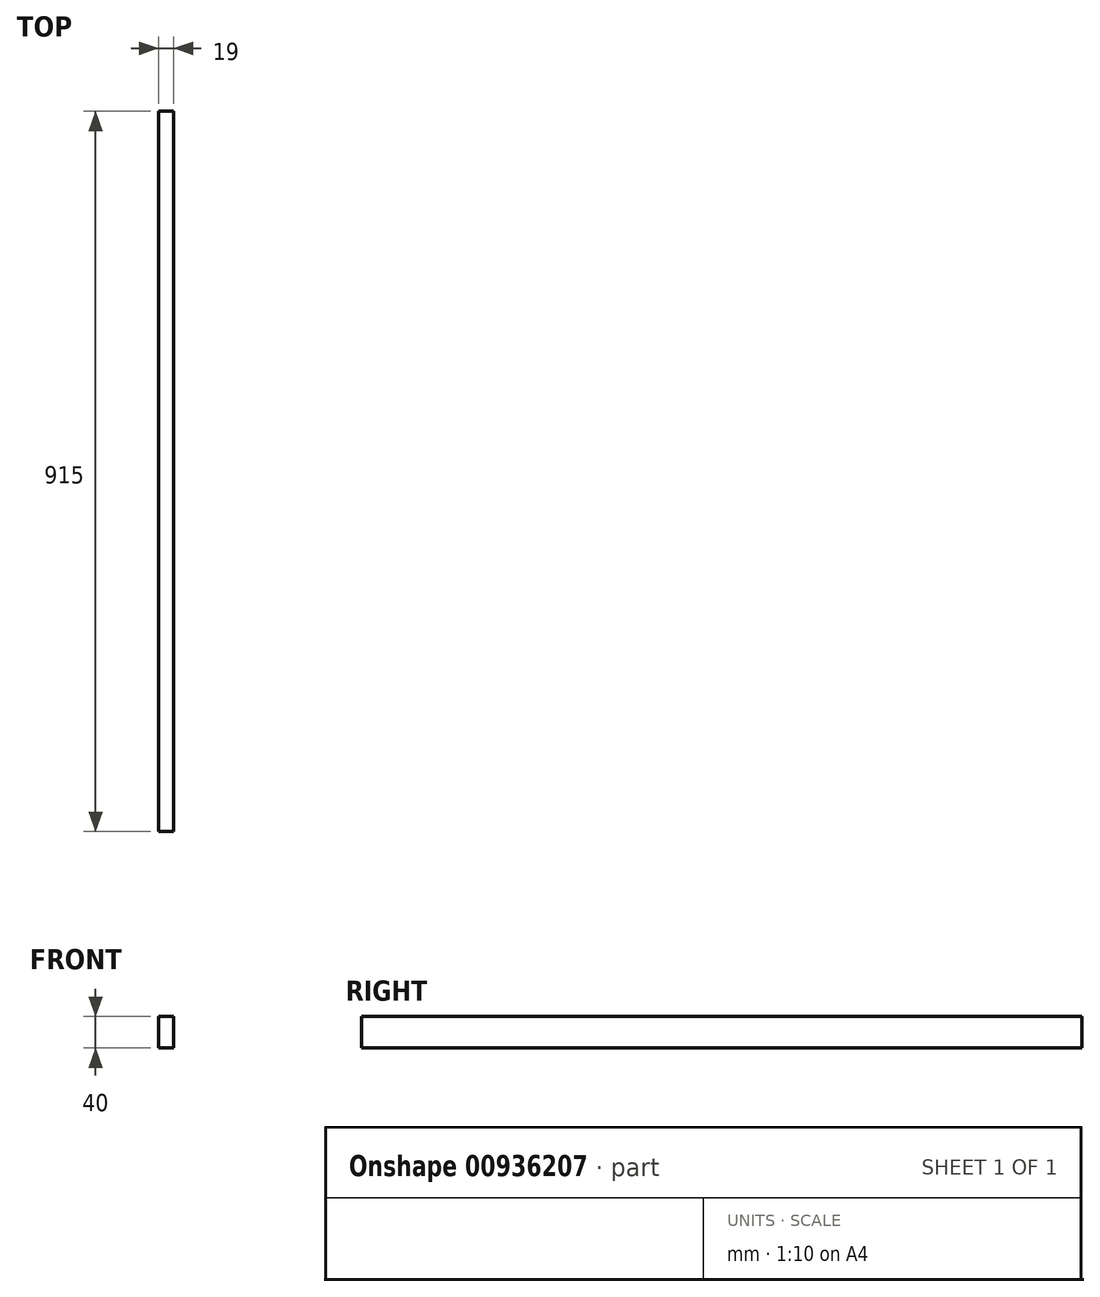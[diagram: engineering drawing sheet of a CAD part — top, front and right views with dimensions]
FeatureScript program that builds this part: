
annotation { "Feature Type Name" : "Feature", "Feature Type Description" : "" }
export const myFeature = defineFeature(function(context is Context, id is Id, definition is map)
    precondition{}
    {
        {
            var Q0;
            Q0=qCreatedBy(makeId("Front.planeOp"),FACE);
            var sketch = newSketch(context, id + "F0", { "sketchPlane" : qUnion([Q0])});
            skLineSegment(sketch, "E0.bottom", {"start": v(0, 0) * mm, "end": v(19, 0) * mm});
            skLineSegment(sketch, "E0.top", {"start": v(0, 40) * mm, "end": v(19, 40) * mm});
            skLineSegment(sketch, "E0.left", {"start": v(0, 0) * mm, "end": v(0, 40) * mm});
            skLineSegment(sketch, "E0.right", {"start": v(19, 0) * mm, "end": v(19, 40) * mm});
            skSolve(sketch);
        }
        {
            var Q0;
            Q0=qSketchRegion(id+"F0",true);
            extrude(context, id + "F1", {"entities" : qUnion([Q0]), "depth" : 915 * mm, "offsetDistance" : 25 * mm});
        }
    });
